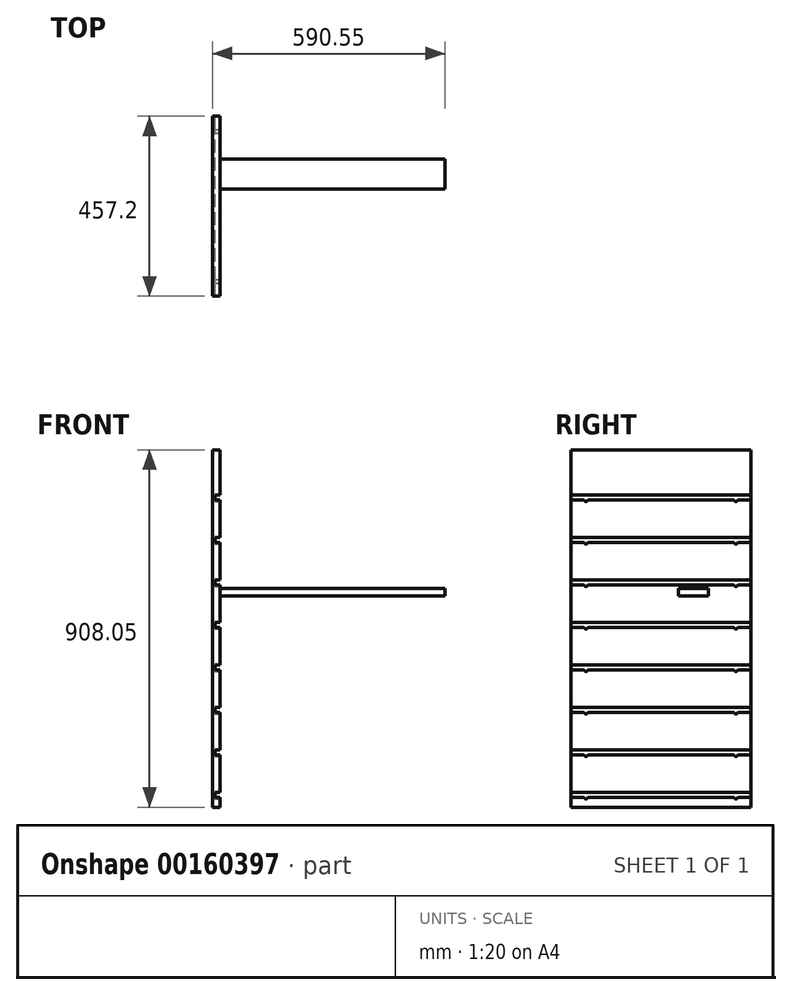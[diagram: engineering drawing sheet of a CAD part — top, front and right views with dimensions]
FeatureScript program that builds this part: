
annotation { "Feature Type Name" : "Feature", "Feature Type Description" : "" }
export const myFeature = defineFeature(function(context is Context, id is Id, definition is map)
    precondition{}
    {
        {
            var Q0;
            Q0=qCreatedBy(makeId("Right.planeOp"),FACE);
            var sketch = newSketch(context, id + "F0", { "sketchPlane" : qUnion([Q0])});
            skLineSegment(sketch, "E0.bottom", {"start": v(-394.71, 459.13) * mm, "end": v(62.49, 459.13) * mm});
            skLineSegment(sketch, "E0.top", {"start": v(-394.71, -448.92) * mm, "end": v(62.49, -448.92) * mm});
            skLineSegment(sketch, "E0.left", {"start": v(-394.71, 459.13) * mm, "end": v(-394.71, -448.92) * mm});
            skLineSegment(sketch, "E0.right", {"start": v(62.49, 459.13) * mm, "end": v(62.49, -448.92) * mm});
            skSolve(sketch);
        }
        {
            var Q0;
            Q0 = qSketchRegion(id + "F0", true);
            var sketch = newSketch(context, id + "F1", { "sketchPlane" : qUnion([Q0])});
            skLineSegment(sketch, "E1.0", {"start": v(-394.71, -423.52) * mm, "end": v(-361.38, -423.52) * mm});
            skLineSegment(sketch, "E2.0", {"start": v(-394.71, -410.82) * mm, "end": v(62.49, -410.82) * mm});
            skLineSegment(sketch, "E3.0", {"start": v(24.39, 459.13) * mm, "end": v(24.39, -448.92) * mm, "construction": true});
            skArc(sketch, "E4", {"start": v(19.62, -423.52) * mm, "mid": v(24.39, -428.28) * mm, "end": v(29.15, -423.52) * mm});
            skLineSegment(sketch, "E5.trimOffspring", {"start": v(29.15, -423.52) * mm, "end": v(62.49, -423.52) * mm});
            skLineSegment(sketch, "E6.0.1.0", {"start": v(29.15, -315.57) * mm, "end": v(62.49, -315.57) * mm});
            skLineSegment(sketch, "E6.0.1.1", {"start": v(-394.71, -302.87) * mm, "end": v(62.49, -302.87) * mm});
            skLineSegment(sketch, "E6.0.1.2", {"start": v(-394.71, -315.57) * mm, "end": v(-361.38, -315.57) * mm});
            skArc(sketch, "E6.0.1.3", {"start": v(19.62, -315.57) * mm, "mid": v(24.39, -320.33) * mm, "end": v(29.15, -315.57) * mm});
            skLineSegment(sketch, "E6.0.2.0", {"start": v(29.15, -207.62) * mm, "end": v(62.49, -207.62) * mm});
            skLineSegment(sketch, "E6.0.2.1", {"start": v(-394.71, -194.92) * mm, "end": v(62.49, -194.92) * mm});
            skLineSegment(sketch, "E6.0.2.2", {"start": v(-394.71, -207.62) * mm, "end": v(-361.38, -207.62) * mm});
            skArc(sketch, "E6.0.2.3", {"start": v(19.62, -207.62) * mm, "mid": v(24.39, -212.38) * mm, "end": v(29.15, -207.62) * mm});
            skLineSegment(sketch, "E6.0.3.0", {"start": v(29.15, -99.67) * mm, "end": v(62.49, -99.67) * mm});
            skLineSegment(sketch, "E6.0.3.1", {"start": v(-394.71, -86.97) * mm, "end": v(62.49, -86.97) * mm});
            skLineSegment(sketch, "E6.0.3.2", {"start": v(-394.71, -99.67) * mm, "end": v(-361.38, -99.67) * mm});
            skArc(sketch, "E6.0.3.3", {"start": v(19.62, -99.67) * mm, "mid": v(24.39, -104.43) * mm, "end": v(29.15, -99.67) * mm});
            skLineSegment(sketch, "E6.0.4.0", {"start": v(29.15, 8.28) * mm, "end": v(62.49, 8.28) * mm});
            skLineSegment(sketch, "E6.0.4.1", {"start": v(-394.71, 20.98) * mm, "end": v(62.49, 20.98) * mm});
            skLineSegment(sketch, "E6.0.4.2", {"start": v(-394.71, 8.28) * mm, "end": v(-361.38, 8.28) * mm});
            skArc(sketch, "E6.0.4.3", {"start": v(19.62, 8.28) * mm, "mid": v(24.39, 3.52) * mm, "end": v(29.15, 8.28) * mm});
            skLineSegment(sketch, "E6.0.5.0", {"start": v(29.15, 116.23) * mm, "end": v(62.49, 116.23) * mm});
            skLineSegment(sketch, "E6.0.5.1", {"start": v(-394.71, 128.93) * mm, "end": v(62.49, 128.93) * mm});
            skLineSegment(sketch, "E6.0.5.2", {"start": v(-394.71, 116.23) * mm, "end": v(-361.38, 116.23) * mm});
            skArc(sketch, "E6.0.5.3", {"start": v(19.62, 116.23) * mm, "mid": v(24.39, 111.47) * mm, "end": v(29.15, 116.23) * mm});
            skLineSegment(sketch, "E6.0.6.0", {"start": v(29.15, 224.18) * mm, "end": v(62.49, 224.18) * mm});
            skLineSegment(sketch, "E6.0.6.1", {"start": v(-394.71, 236.88) * mm, "end": v(62.49, 236.88) * mm});
            skLineSegment(sketch, "E6.0.6.2", {"start": v(-394.71, 224.18) * mm, "end": v(-361.38, 224.18) * mm});
            skArc(sketch, "E6.0.6.3", {"start": v(19.62, 224.18) * mm, "mid": v(24.39, 219.42) * mm, "end": v(29.15, 224.18) * mm});
            skLineSegment(sketch, "E6.0.7.0", {"start": v(29.15, 332.13) * mm, "end": v(62.49, 332.13) * mm});
            skLineSegment(sketch, "E6.0.7.1", {"start": v(-394.71, 344.83) * mm, "end": v(62.49, 344.83) * mm});
            skLineSegment(sketch, "E6.0.7.2", {"start": v(-394.71, 332.13) * mm, "end": v(-361.38, 332.13) * mm});
            skArc(sketch, "E6.0.7.3", {"start": v(19.62, 332.13) * mm, "mid": v(24.39, 327.37) * mm, "end": v(29.15, 332.13) * mm});
            skLineSegment(sketch, "E6.direction1", {"start": v(-394.71, -410.82) * mm, "end": v(-369.31, -410.82) * mm, "construction": true});
            skLineSegment(sketch, "E6.direction2", {"start": v(-394.71, -410.82) * mm, "end": v(-394.71, -302.87) * mm, "construction": true});
            skLineSegment(sketch, "E7.0", {"start": v(-356.61, 459.13) * mm, "end": v(-356.61, -448.92) * mm, "construction": true});
            skArc(sketch, "E8", {"start": v(-361.38, 332.13) * mm, "mid": v(-356.61, 327.37) * mm, "end": v(-351.85, 332.13) * mm});
            skLineSegment(sketch, "E9.trimOffspring", {"start": v(-351.85, 332.13) * mm, "end": v(19.62, 332.13) * mm});
            skArc(sketch, "E10", {"start": v(-361.38, 224.18) * mm, "mid": v(-356.61, 219.42) * mm, "end": v(-351.85, 224.18) * mm});
            skArc(sketch, "E11", {"start": v(-361.38, 116.23) * mm, "mid": v(-356.61, 111.47) * mm, "end": v(-351.85, 116.23) * mm});
            skArc(sketch, "E12", {"start": v(-361.38, 8.28) * mm, "mid": v(-356.61, 3.52) * mm, "end": v(-351.85, 8.28) * mm});
            skPoint(sketch, "E12.centerSnap0", {"position": v(-356.61, 5.1) * mm});
            skArc(sketch, "E13", {"start": v(-361.38, -99.67) * mm, "mid": v(-356.61, -104.43) * mm, "end": v(-351.85, -99.67) * mm});
            skArc(sketch, "E14", {"start": v(-361.38, -207.62) * mm, "mid": v(-356.61, -212.38) * mm, "end": v(-351.85, -207.62) * mm});
            skArc(sketch, "E15", {"start": v(-361.38, -315.57) * mm, "mid": v(-356.61, -320.33) * mm, "end": v(-351.85, -315.57) * mm});
            skArc(sketch, "E16", {"start": v(-361.38, -423.52) * mm, "mid": v(-356.61, -428.28) * mm, "end": v(-351.85, -423.52) * mm});
            skLineSegment(sketch, "E17.trimOffspring", {"start": v(-351.85, 224.18) * mm, "end": v(19.62, 224.18) * mm});
            skLineSegment(sketch, "E18.trimOffspring", {"start": v(-351.85, 116.23) * mm, "end": v(19.62, 116.23) * mm});
            skLineSegment(sketch, "E19.trimOffspring", {"start": v(-351.85, 8.28) * mm, "end": v(19.62, 8.28) * mm});
            skLineSegment(sketch, "E20.trimOffspring", {"start": v(-351.85, -99.67) * mm, "end": v(19.62, -99.67) * mm});
            skLineSegment(sketch, "E21.trimOffspring", {"start": v(-351.85, -207.62) * mm, "end": v(19.62, -207.62) * mm});
            skLineSegment(sketch, "E22.trimOffspring", {"start": v(-351.85, -315.57) * mm, "end": v(19.62, -315.57) * mm});
            skLineSegment(sketch, "E23.trimOffspring", {"start": v(-351.85, -423.52) * mm, "end": v(19.62, -423.52) * mm});
            skSolve(sketch);
        }
        {
            var Q0;
            Q0=makeQuery(id+"F0.imprint","IMPRINT",FACE,{"disambiguationData":[TD([[makeQuery(id+"F0.imprint","IMPRINT",EDGE,{"derivedFrom":sQuery(id+"F0.wireOp",EDGE,"E0.bottom")}),-1.0]])]});
            extrude(context, id + "F2", {"entities" : qUnion([Q0]), "oppositeDirection" : true, "depth" : 19.05 * mm});
        }
        {
            var Q0;
            {var subQ2=sQuery(id+"F1.wireOp",EDGE,"E1.0");Q0=makeQuery(id+"F1.imprint","IMPRINT",FACE,{"disambiguationData":[TD([[makeQuery(id+"F1.imprint","IMPRINT",EDGE,{"derivedFrom":subQ2}),1.0]])]});}
            extrude(context, id + "F3", {"entities" : qUnion([Q0]), "operationType" : NewBodyOperationType.REMOVE, "oppositeDirection" : true, "depth" : 12.7 * mm});
        }
        {
            var Q0;
            {var subQ2=sQuery(id+"F1.wireOp",EDGE,"E6.0.1.0");Q0=makeQuery(id+"F1.imprint","IMPRINT",FACE,{"disambiguationData":[TD([[makeQuery(id+"F1.imprint","IMPRINT",EDGE,{"derivedFrom":subQ2}),1.0]])]});}
            var Q1;
            {var subQ2=sQuery(id+"F1.wireOp",EDGE,"E6.0.2.0");Q1=makeQuery(id+"F1.imprint","IMPRINT",FACE,{"disambiguationData":[TD([[makeQuery(id+"F1.imprint","IMPRINT",EDGE,{"derivedFrom":subQ2}),1.0]])]});}
            var Q2;
            {var subQ2=sQuery(id+"F1.wireOp",EDGE,"E6.0.3.0");Q2=makeQuery(id+"F1.imprint","IMPRINT",FACE,{"disambiguationData":[TD([[makeQuery(id+"F1.imprint","IMPRINT",EDGE,{"derivedFrom":subQ2}),1.0]])]});}
            var Q3;
            {var subQ2=sQuery(id+"F1.wireOp",EDGE,"E6.0.4.0");Q3=makeQuery(id+"F1.imprint","IMPRINT",FACE,{"disambiguationData":[TD([[makeQuery(id+"F1.imprint","IMPRINT",EDGE,{"derivedFrom":subQ2}),1.0]])]});}
            var Q4;
            {var subQ2=sQuery(id+"F1.wireOp",EDGE,"E6.0.5.0");Q4=makeQuery(id+"F1.imprint","IMPRINT",FACE,{"disambiguationData":[TD([[makeQuery(id+"F1.imprint","IMPRINT",EDGE,{"derivedFrom":subQ2}),1.0]])]});}
            var Q5;
            {var subQ2=sQuery(id+"F1.wireOp",EDGE,"E6.0.6.0");Q5=makeQuery(id+"F1.imprint","IMPRINT",FACE,{"disambiguationData":[TD([[makeQuery(id+"F1.imprint","IMPRINT",EDGE,{"derivedFrom":subQ2}),1.0]])]});}
            var Q6;
            {var subQ2=sQuery(id+"F1.wireOp",EDGE,"E6.0.7.0");Q6=makeQuery(id+"F1.imprint","IMPRINT",FACE,{"disambiguationData":[TD([[makeQuery(id+"F1.imprint","IMPRINT",EDGE,{"derivedFrom":subQ2}),1.0]])]});}
            var Q7;
            Q7 = qBodyType(qCreatedBy(id + "F1" ,EDGE), BodyType.WIRE);
            var Q8;
            Q8=sQuery(id+"F1.wireOp",EDGE,"E6.0.1.2");
            extrude(context, id + "F4", {"entities" : qUnion([Q0, Q1, Q2, Q3, Q4, Q5, Q6]), "operationType" : NewBodyOperationType.REMOVE, "surfaceEntities" : qUnion([Q7, Q8]), "oppositeDirection" : true, "depth" : 12.7 * mm});
        }
        {
            var Q0;
            Q0=qCreatedBy(makeId("Right.planeOp"),FACE);
            var sketch = newSketch(context, id + "F5", { "sketchPlane" : qUnion([Q0])});
            skLineSegment(sketch, "E24.bottom", {"start": v(-45.84, 87.35) * mm, "end": v(-122.04, 87.35) * mm});
            skLineSegment(sketch, "E24.top", {"start": v(-45.84, 106.4) * mm, "end": v(-122.04, 106.4) * mm});
            skLineSegment(sketch, "E24.left", {"start": v(-45.84, 87.35) * mm, "end": v(-45.84, 106.4) * mm});
            skLineSegment(sketch, "E24.right", {"start": v(-122.04, 87.35) * mm, "end": v(-122.04, 106.4) * mm});
            skSolve(sketch);
        }
        {
            var Q0;
            Q0 = qSketchRegion(id + "F5", true);
            extrude(context, id + "F6", {"entities" : qUnion([Q0]), "depth" : 571.5 * mm});
        }
    });
